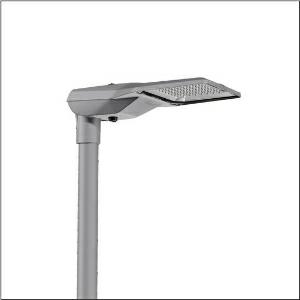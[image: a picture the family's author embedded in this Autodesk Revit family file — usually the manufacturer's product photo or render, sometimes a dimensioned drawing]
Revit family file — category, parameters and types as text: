
# Revit family: streetlight_sl_21_midi___st0_5a_5xe3b33t08lb_a6fa
name_source: partatom
category: Lighting Fixtures
units: mm (PartAtom-declared; Revit-internal decimal feet)

## family parameters
Cut with Voids When Loaded = No
Host = Face
Light Source = No
Part Type = Normal
Room Calculation Point = No
Round Connector Dimension = Use Diameter
Shared = No

## types (1)
- --- (1 x LED, 14340 lm, 99.6 W, 3000K)
    Apparent Load = 100 VA
    CIE Flux Codes = 41 75 97 100 100
    Color Rendering = 70
    Color Temperature = 3000K
    Default Elevation = 1800 mm
    Description = Streetlight SL 21 midi, mast luminaire, primary light control with lens, of PMMA, primary optical cover: cover, of toughened safety glass, transparent, light distribution: ST0.5a, light emission: direct distribution, primary light characteristic: asymmetric, installation type: side-entry, post-top, LED, High Power LED, rated luminous flux: 14.340lm, luminous efficacy: 144lm/W, light colour: 730, colour temperature: 3000K, control gear: D4i, control: overheat protection, constant luminous flux control, time-dependent luminous flux control, flexible luminous flux parameterisation, pre-setting: logarithmic dimming characteristic, mains connection: 230..240V, AC, 50/60Hz, start of lifetime: 100W, end of service life: 102W, reduction: 46W, luminaire housing, of diecast aluminium, powder-coated, Siteco® metallic grey (DB 702S), corrosivity category C5 mid according to DIN EN ISO 12944, please order mast flange separately, inclination adjustable: 0°, 5°, 10°, 15°, sealing non-destructively replaceable, multi-level sealing system, length: 644mm, width: 335mm, height: 110mm, mast flange for spigot size: 42mm (side-entry): 5XC10008XM4, 60/48mm (side-entry/post-top): 5XC10108XM2, 76/60mm (side-entry/post-top): 5XC10108XM1, mounting height: 4..8m, Smart Interface below and above, protection rating (complete): IP66, insulation class (complete): insulation class II (safety insulation), certification: CE, ENEC, ENEC+, VDE, impact resistance: IK10, permissible operating ambient temperature for outdoor applications: -40..+50°C, standard-compliant lighting for roads and squares, packaging unit: 1 piece

Light Distribution: ST0.5a
    Height = 111 mm
    Lamp = 1 x LED
    Lamp Light Flux = 14340 lm
    Lamp Power = 99.6 W
    Lamp count = 1
    Length = 644 mm
    Luminous efficacy = 144 lm/W
    Manufacturer = Siteco
    ModVariant = No
    Model = 5XE3B33T08LB
    Number of Poles = 1
    OnlyDefault = Yes
    Power Factor = 1
    Product Name = Streetlight SL 21 midi | ST0.5a
    Product group = mast luminaire | pylon top
    ProductGroupID = 6100
    Protection Class = Protection class II
    Protection Degree = IP 66
    RLX_Detail_Level = 1
    RLX_Emergency_Light_Flux = 0 lm
    RLX_Emergency_Type = 0
    RLX_Emergency_Type_DB = No
    RlxData = <blob elided: 38001 chars, md5=f5cd1afe>
    Socket = socket
    Standby Power = 0 W
    System Light Flux = 14340 lm
    System Power = 100 W
    Type Comments = factory setting: luminous flux: 100 % | dim-lin: 254 | 1020 mA
    Type Image = l_1004304.jpg
    URL = http://relux.com
    VarID = @adj_012631
    Voltage = 0 V
    Weight = 0.00 kg
    Width = 336 mm

## geometry (parser evidence)
native form markers: Blend x4, Sweep x11
no freeform markers — native parametric forms only
